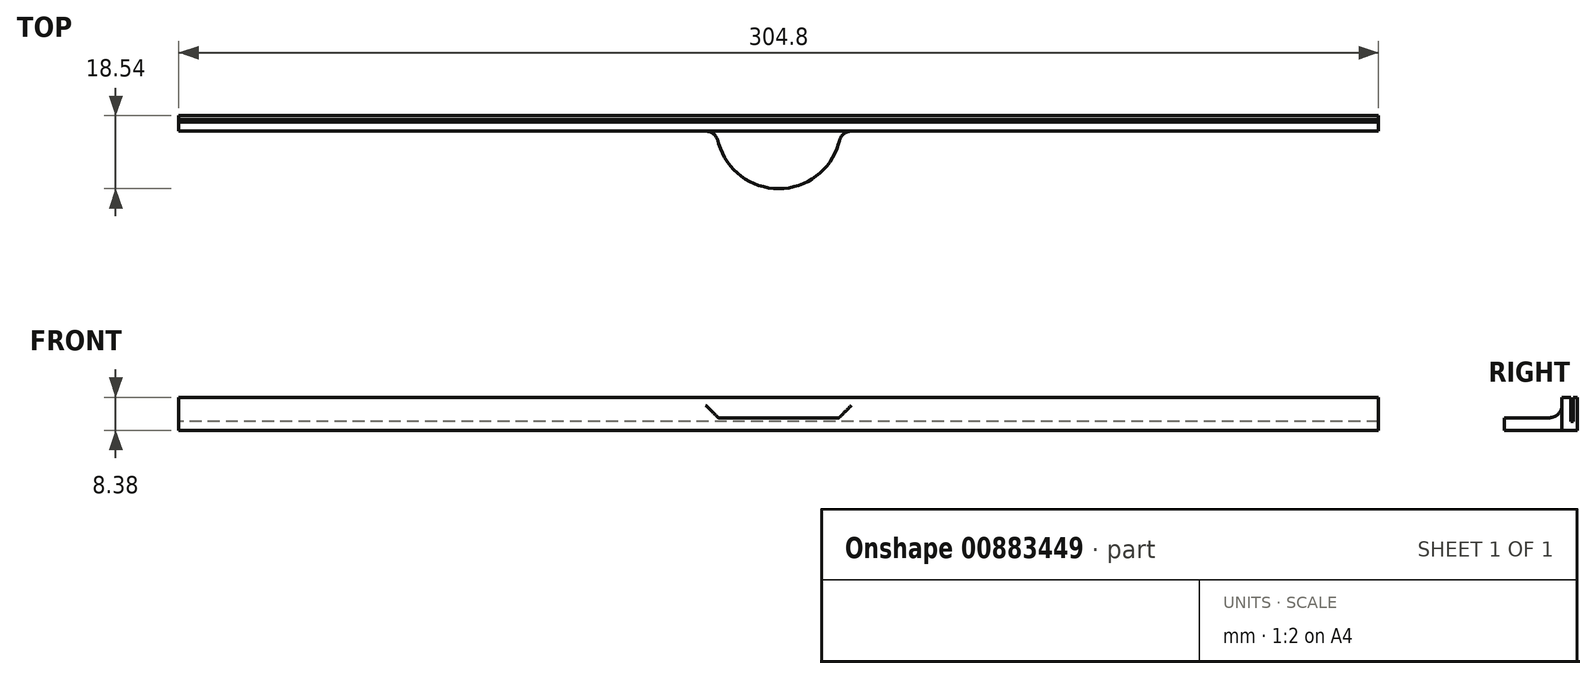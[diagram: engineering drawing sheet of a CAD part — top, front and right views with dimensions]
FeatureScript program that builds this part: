
annotation { "Feature Type Name" : "Feature", "Feature Type Description" : "" }
export const myFeature = defineFeature(function(context is Context, id is Id, definition is map)
    precondition{}
    {
        {
            var Q0;
            Q0=qCreatedBy(makeId("Right.planeOp"),FACE);
            var sketch = newSketch(context, id + "F0", { "sketchPlane" : qUnion([Q0])});
            skLineSegment(sketch, "E0.bottom", {"start": v(0, 0) * mm, "end": v(-2.67, 0) * mm});
            skLineSegment(sketch, "E0.top", {"start": v(0, 6.35) * mm, "end": v(-1.02, 6.35) * mm});
            skLineSegment(sketch, "E0.left", {"start": v(0, 0) * mm, "end": v(0, 6.35) * mm});
            skLineSegment(sketch, "E0.right", {"start": v(-2.67, 0) * mm, "end": v(-2.67, 6.35) * mm});
            skLineSegment(sketch, "E1.top", {"start": v(-1.65, 0.25) * mm, "end": v(-1.02, 0.25) * mm});
            skLineSegment(sketch, "E1.left", {"start": v(-1.65, 6.35) * mm, "end": v(-1.65, 0.25) * mm});
            skLineSegment(sketch, "E1.right", {"start": v(-1.02, 6.35) * mm, "end": v(-1.02, 0.25) * mm});
            skLineSegment(sketch, "E2.trimOffspring", {"start": v(-1.65, 6.35) * mm, "end": v(-2.67, 6.35) * mm});
            skSolve(sketch);
        }
        {
            var Q0;
            Q0=qSketchRegion(id+"F0",true);
            extrude(context, id + "F1", {"entities" : qUnion([Q0]), "depth" : 304.8 * mm, "offsetDistance" : 25.4 * mm});
        }
        {
            var Q0;
            Q0=makeQuery(id+"F1.opExtrude","SWEPT_FACE",FACE,{"disambiguationData":[OSD([sQuery(id+"F0.wireOp",EDGE,"E0.bottom")])]});
            extrude(context, id + "F2", {"entities" : qUnion([Q0]), "operationType" : NewBodyOperationType.ADD, "depth" : 2.03 * mm, "offsetDistance" : 25.4 * mm});
        }
        {
            var Q0;
            Q0=makeQuery(id+"F2.opExtrude","CAP_FACE",FACE,{"disambiguationData":[OSD([sQuery(id+"F0.wireOp",EDGE,"E0.bottom")])],"isStart":false});
            var sketch = newSketch(context, id + "F3", { "sketchPlane" : qUnion([Q0])});
            skArc(sketch, "E3", {"start": v(168.28, 2.67) * mm, "mid": v(152.4, 18.54) * mm, "end": v(136.53, 2.67) * mm});
            skLineSegment(sketch, "E4.0", {"start": v(168.28, 2.67) * mm, "end": v(136.53, 2.67) * mm});
            skPoint(sketch, "E5.orphan", {"position": v(0, 2.67) * mm});
            skPoint(sketch, "E6.orphan", {"position": v(304.8, 2.67) * mm});
            skSolve(sketch);
        }
        {
            var Q0;
            {var subQ0=sQuery(id+"F0.wireOp",EDGE,"E0.right");Q0=makeQuery(id+"F2.boolean.opBoolean","MERGE",FACE,{"derivedFrom":[makeQuery(id+"F1.opExtrude","SWEPT_FACE",FACE,{"disambiguationData":[OSD([subQ0])]}),makeQuery(id+"F2.opExtrude","SWEPT_FACE",FACE,{"disambiguationData":[OSD([sQuery(id+"F0.wireOp",EDGE,"E0.bottom"),subQ0])]})]});}
            extrude(context, id + "F4", {"entities" : qUnion([Q0]), "operationType" : NewBodyOperationType.ADD, "depth" : 1.27 * mm, "offsetDistance" : 25.4 * mm});
        }
        {
            var Q0;
            Q0 = qSketchRegion(id + "F3", true);
            extrude(context, id + "F5", {"entities" : qUnion([Q0]), "operationType" : NewBodyOperationType.ADD, "oppositeDirection" : true, "depth" : 3.17 * mm, "offsetDistance" : 25.4 * mm});
        }
        {
            var Q0;
            Q0=makeQuery(id+"F5.boolean.opBoolean","INTERSECT",EDGE,{"derivedFrom":[makeQuery(id+"F4.opExtrude","CAP_FACE",FACE,{"disambiguationData":[OSD([sQuery(id+"F0.wireOp",EDGE,"E0.bottom"),sQuery(id+"F0.wireOp",EDGE,"E0.right")])],"isStart":false}),makeQuery(id+"F5.opExtrude","CAP_FACE",FACE,{"disambiguationData":[OSD([sQuery(id+"F3.wireOp",EDGE,"E3"),sQuery(id+"F3.wireOp",EDGE,"E4.0")])],"isStart":false})]});
            var Q1;
            Q1=makeQuery(id+"F5.boolean.opBoolean","INTERSECT",EDGE,{"disambiguationData":[OD(1.0)],"derivedFrom":[makeQuery(id+"F4.opExtrude","CAP_FACE",FACE,{"disambiguationData":[OSD([sQuery(id+"F0.wireOp",EDGE,"E0.bottom"),sQuery(id+"F0.wireOp",EDGE,"E0.right")])],"isStart":false}),makeQuery(id+"F5.opExtrude","SWEPT_FACE",FACE,{"disambiguationData":[OSD([sQuery(id+"F3.wireOp",EDGE,"E3")])]})]});
            var Q2;
            Q2=makeQuery(id+"F5.boolean.opBoolean","INTERSECT",EDGE,{"disambiguationData":[OD(0.0)],"derivedFrom":[makeQuery(id+"F4.opExtrude","CAP_FACE",FACE,{"disambiguationData":[OSD([sQuery(id+"F0.wireOp",EDGE,"E0.bottom"),sQuery(id+"F0.wireOp",EDGE,"E0.right")])],"isStart":false}),makeQuery(id+"F5.opExtrude","SWEPT_FACE",FACE,{"disambiguationData":[OSD([sQuery(id+"F3.wireOp",EDGE,"E3")])]})]});
            fillet(context, id + "F6", {"entities" : qUnion([Q0, Q1, Q2]), "radius" : 3.17 * mm, "tangentPropagation" : true, "allowEdgeOverflow" : false});
        }
    });
